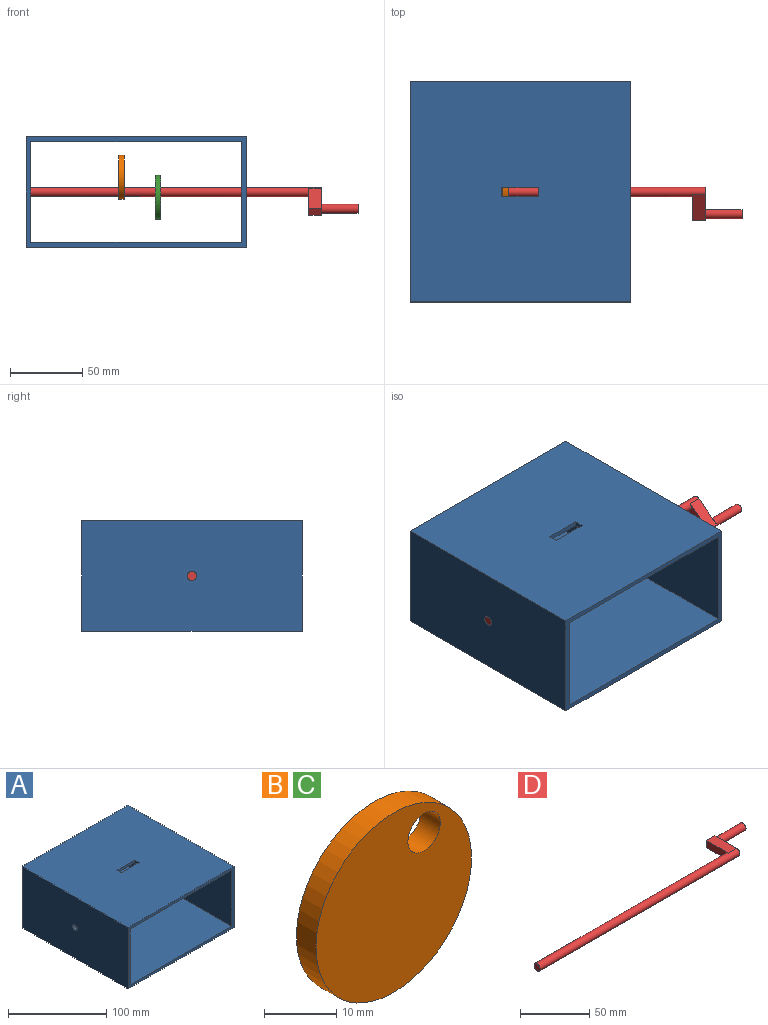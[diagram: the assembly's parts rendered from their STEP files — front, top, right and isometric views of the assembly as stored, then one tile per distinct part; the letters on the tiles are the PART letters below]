
ASSEMBLY  parts=4 mates=3
PART A: 16 faces, bbox 152.4x152.4x76.2 mm
  f0: plane 152.4x152.4mm, normal (0,0,1), area 23064.5mm2, adj f2,f4,f5,f6,f12,f13,f14,f15
  f1: plane 152.4x145.8mm, normal (0,0,-1), area 22058mm2, adj f5,f6,f7,f8,f12,f13,f14,f15
  f2: plane 152.4x76.2mm, normal (-1,0,0), area 11581.2mm2, adj f0,f3,f5,f6,f10
  f3: plane 152.4x152.4mm, normal (0,0,-1), area 23225.8mm2, adj f2,f4,f5,f6
  f4: plane 152.4x76.2mm, normal (1,0,0), area 11581.2mm2, adj f0,f3,f5,f6,f11
  f5: plane 152.4x76.2mm, normal (0,-1,0), area 1466.1mm2, adj f0,f1,f2,f3,f4,f7,f8,f9
  f6: plane 152.4x76.2mm, normal (0,1,0), area 1466.1mm2, adj f0,f1,f2,f3,f4,f7,f8,f9
  f7: plane 152.4x69.6mm, normal (-1,0,0), area 10574.8mm2, adj f1,f5,f6,f9,f11
  f8: plane 152.4x69.6mm, normal (1,0,0), area 10574.8mm2, adj f1,f5,f6,f9,f10
  f9: plane 152.4x145.8mm, normal (0,0,1), area 22219.3mm2, adj f5,f6,f7,f8
  f10: cylinder r=3.17mm len=6.35mm, axis (-1,0,0), area 65.9mm2, adj f2,f8
  f11: cylinder r=3.17mm len=6.35mm, axis (-1,0,0), area 65.9mm2, adj f4,f7
  f12: plane 25.4x3.3mm, normal (0,1,0), area 83.9mm2, adj f0,f1,f13,f15
  f13: plane 6.35x3.3mm, normal (-1,0,0), area 21mm2, adj f0,f1,f12,f14
  f14: plane 25.4x3.3mm, normal (0,-1,0), area 83.9mm2, adj f0,f1,f13,f15
  f15: plane 6.35x3.3mm, normal (1,0,0), area 21mm2, adj f0,f1,f12,f14
PART B: 4 faces, bbox 30.5x3.8x30.5 mm
  f0: cylinder r=3.17mm len=6.35mm, axis (0,1,0), area 76mm2, adj f2,f3
  f1: cylinder r=15.23mm len=30.46mm, axis (0,1,0), area 364.6mm2, adj f2,f3
  f2: plane 30.46x30.46mm, normal (0,-1,0), area 696.9mm2, adj f0,f1
  f3: plane 30.46x30.46mm, normal (0,1,0), area 696.9mm2, adj f0,f1
PART C: same geometry as B
PART D: 11 faces, bbox 229.9x25.6x6.4 mm
  f0: plane 3.18x3.18mm, normal (1,0,0), area 2.2mm2, adj f6,f7,f9
  f1: plane 3.18x3.18mm, normal (1,0,0), area 2.2mm2, adj f5,f7,f9
  f2: cylinder r=3.17mm len=204.47mm, axis (-1,0,0), area 3992.9mm2, adj f3,f4,f5,f6,f8
  f3: plane 6.35x6.35mm, normal (-1,0,0), area 31.7mm2, adj f2
  f4: plane 22.43x6.35mm, normal (-1,0,0), area 126.6mm2, adj f2,f5,f6,f7
  f5: plane 22.43x8.64mm, normal (0,0,1), area 193.7mm2, adj f1,f2,f4,f7,f8
  f6: plane 22.43x8.64mm, normal (0,0,-1), area 193.7mm2, adj f0,f2,f4,f7,f8
  f7: plane 8.64x6.35mm, normal (0,1,0), area 54.8mm2, adj f0,f1,f4,f5,f6
  f8: plane 22.43x6.35mm, normal (1,0,0), area 122.2mm2, adj f2,f5,f6,f9
  f9: cylinder r=3.17mm len=25.4mm, axis (-1,0,0), area 506.7mm2, adj f0,f1,f8,f10
  f10: plane 6.35x6.35mm, normal (1,0,0), area 31.7mm2, adj f9
PLACE A t=(-30.37,92.31,-121.85)mm fixed
PLACE B rot(axis=(0.67,0.67,-0.33),143.5deg) t=(37.57,19.63,-73.57)mm
PLACE C rot(axis=(0.31,0.31,-0.9),95.9deg) t=(62.97,26.29,-87.27)mm
PLACE D rot(axis=(-1,0,0),142.6deg) t=(-53.23,-67.56,-99.77)mm
MATE revolute A.f10 <-> D.f2  axis (-1,0,0) through (-30.37,16.11,-83.75)mm
MATE fastened B.f0 <-> D.f2  axis (-1,0,0) through (33.76,16.11,-83.75)mm
MATE fastened C.f0 <-> D.f2  axis (-1,0,0) through (59.16,16.11,-83.75)mm
